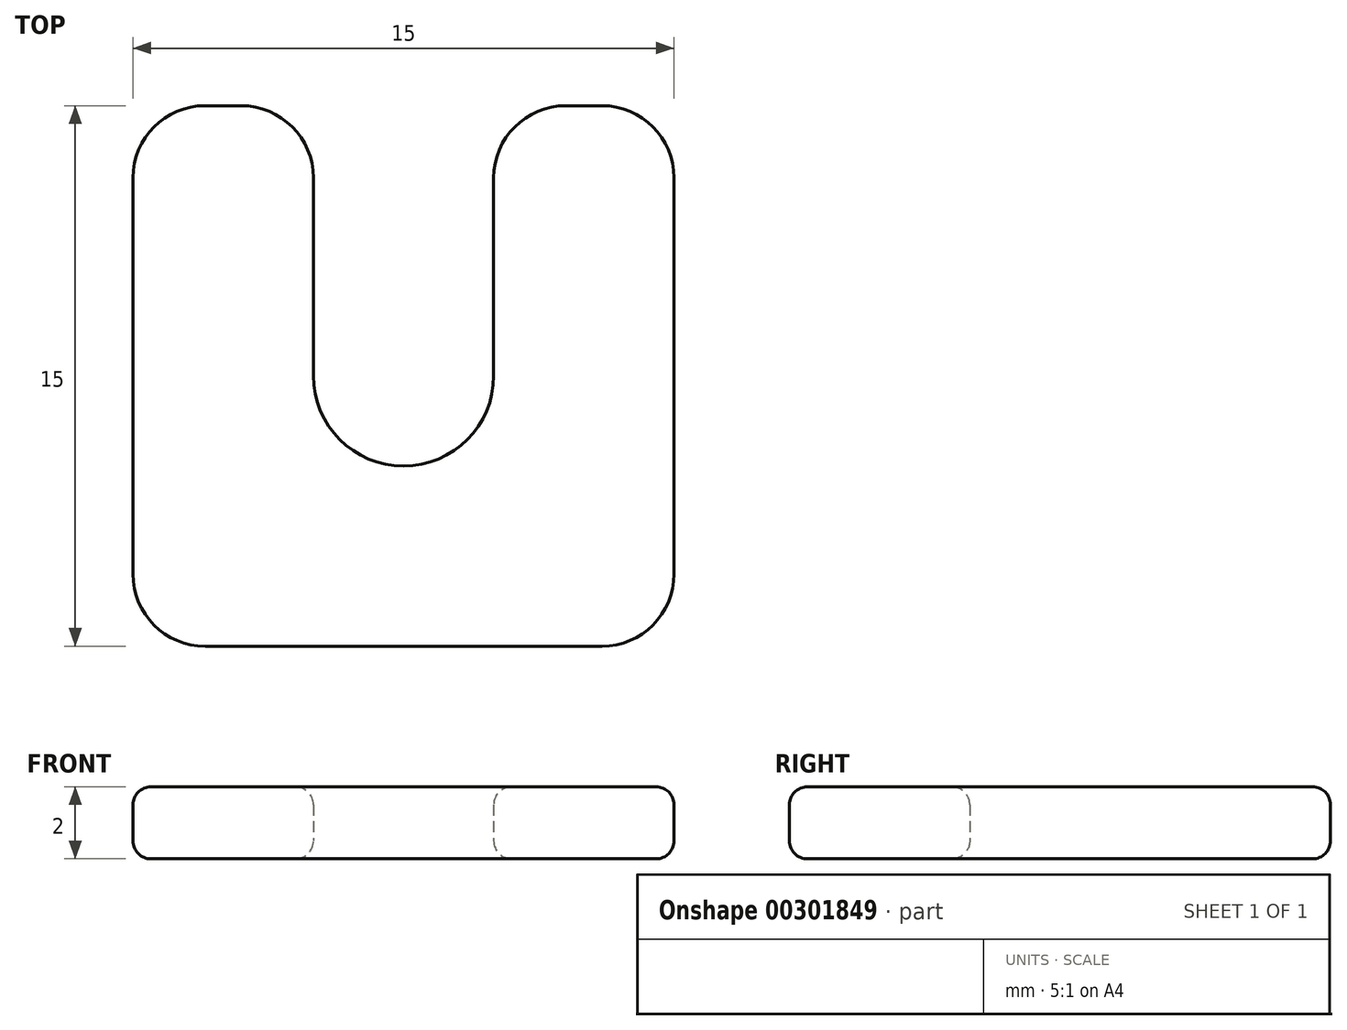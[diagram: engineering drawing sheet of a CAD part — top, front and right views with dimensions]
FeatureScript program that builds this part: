
annotation { "Feature Type Name" : "Feature", "Feature Type Description" : "" }
export const myFeature = defineFeature(function(context is Context, id is Id, definition is map)
    precondition{}
    {
        {
            var Q0;
            Q0=qCreatedBy(makeId("Top.planeOp"),FACE);
            var sketch = newSketch(context, id + "F0", { "sketchPlane" : qUnion([Q0])});
            skCircle(sketch, "E0", {"center": v(0, 0) * mm, "radius": 2.5 * mm});
            skLineSegment(sketch, "E1.bottom", {"start": v(7.5, -7.5) * mm, "end": v(-7.5, -7.5) * mm});
            skLineSegment(sketch, "E1.top", {"start": v(7.5, 7.5) * mm, "end": v(-7.5, 7.5) * mm});
            skLineSegment(sketch, "E1.left", {"start": v(7.5, -7.5) * mm, "end": v(7.5, 7.5) * mm});
            skLineSegment(sketch, "E1.right", {"start": v(-7.5, -7.5) * mm, "end": v(-7.5, 7.5) * mm});
            skLineSegment(sketch, "E2", {"start": v(0, 0) * mm, "end": v(-7.5, 0) * mm, "construction": true});
            skLineSegment(sketch, "E3", {"start": v(0, 0) * mm, "end": v(7.5, 0) * mm, "construction": true});
            skLineSegment(sketch, "E4", {"start": v(-2.5, 0) * mm, "end": v(-2.5, 7.5) * mm});
            skLineSegment(sketch, "E5", {"start": v(2.5, 0) * mm, "end": v(2.5, 7.5) * mm});
            skSolve(sketch);
        }
        {
            var Q0;
            Q0=makeQuery(id+"F0.imprint","IMPRINT",FACE,{"disambiguationData":[TD([[makeQuery(id+"F0.imprint","IMPRINT",EDGE,{"derivedFrom":sQuery(id+"F0.wireOp",EDGE,"E1.bottom")}),-1.0]])]});
            extrude(context, id + "F1", {"entities" : qUnion([Q0]), "depth" : 2 * mm});
        }
        {
            var Q0;
            Q0=makeQuery(id+"F1.opExtrude","SWEPT_EDGE",EDGE,{"disambiguationData":[OSD([sQuery(id+"F0.wireOp",EDGE,"E1.bottom"),sQuery(id+"F0.wireOp",EDGE,"E1.left")])]});
            var Q1;
            Q1=makeQuery(id+"F1.opExtrude","SWEPT_EDGE",EDGE,{"disambiguationData":[OSD([sQuery(id+"F0.wireOp",EDGE,"E1.bottom"),sQuery(id+"F0.wireOp",EDGE,"E1.right")])]});
            var Q2;
            Q2=makeQuery(id+"F1.opExtrude","SWEPT_EDGE",EDGE,{"disambiguationData":[OSD([sQuery(id+"F0.wireOp",EDGE,"E1.top"),sQuery(id+"F0.wireOp",EDGE,"E1.left")])]});
            var Q3;
            Q3=makeQuery(id+"F1.opExtrude","SWEPT_EDGE",EDGE,{"disambiguationData":[OSD([sQuery(id+"F0.wireOp",EDGE,"E1.top"),sQuery(id+"F0.wireOp",EDGE,"E5")])]});
            var Q4;
            Q4=makeQuery(id+"F1.opExtrude","SWEPT_EDGE",EDGE,{"disambiguationData":[OSD([sQuery(id+"F0.wireOp",EDGE,"E1.top"),sQuery(id+"F0.wireOp",EDGE,"E4")])]});
            var Q5;
            Q5=makeQuery(id+"F1.opExtrude","SWEPT_EDGE",EDGE,{"disambiguationData":[OSD([sQuery(id+"F0.wireOp",EDGE,"E1.top"),sQuery(id+"F0.wireOp",EDGE,"E1.right")])]});
            fillet(context, id + "F2", {"entities" : qUnion([Q0, Q1, Q2, Q3, Q4, Q5]), "radius" : 2 * mm, "tangentPropagation" : true, "allowEdgeOverflow" : false});
        }
        {
            var Q0;
            Q0=makeQuery(id+"F1.opExtrude","CAP_FACE",FACE,{"disambiguationData":[OSD([sQuery(id+"F0.wireOp",EDGE,"E0"),sQuery(id+"F0.wireOp",EDGE,"E1.bottom"),sQuery(id+"F0.wireOp",EDGE,"E1.top"),sQuery(id+"F0.wireOp",EDGE,"E1.left"),sQuery(id+"F0.wireOp",EDGE,"E1.right"),sQuery(id+"F0.wireOp",EDGE,"E4"),sQuery(id+"F0.wireOp",EDGE,"E5")])],"isStart":false});
            var Q1;
            Q1=makeQuery(id+"F1.opExtrude","CAP_FACE",FACE,{"disambiguationData":[OSD([sQuery(id+"F0.wireOp",EDGE,"E0"),sQuery(id+"F0.wireOp",EDGE,"E1.bottom"),sQuery(id+"F0.wireOp",EDGE,"E1.top"),sQuery(id+"F0.wireOp",EDGE,"E1.left"),sQuery(id+"F0.wireOp",EDGE,"E1.right"),sQuery(id+"F0.wireOp",EDGE,"E4"),sQuery(id+"F0.wireOp",EDGE,"E5")])],"isStart":true});
            fillet(context, id + "F3", {"entities" : qUnion([Q0, Q1]), "radius" : 0.5 * mm, "tangentPropagation" : true, "allowEdgeOverflow" : false});
        }
    });
